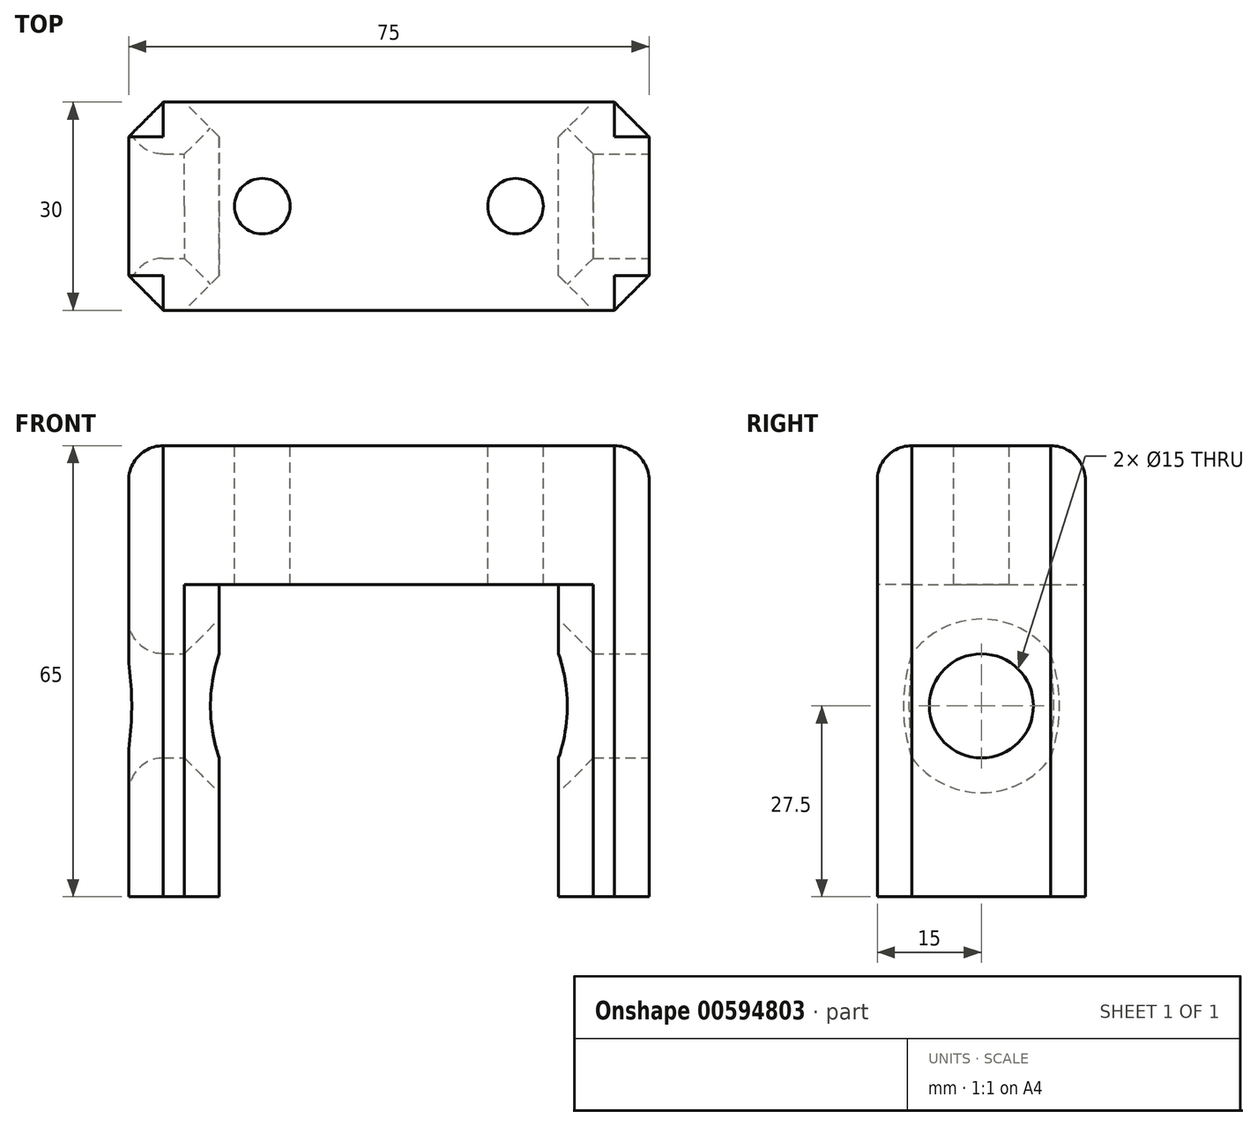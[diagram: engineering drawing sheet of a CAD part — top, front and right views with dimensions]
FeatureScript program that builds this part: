
annotation { "Feature Type Name" : "Feature", "Feature Type Description" : "" }
export const myFeature = defineFeature(function(context is Context, id is Id, definition is map)
    precondition{}
    {
        {
            var Q0;
            Q0=qCreatedBy(makeId("Front.planeOp"),FACE);
            var sketch = newSketch(context, id + "F0", { "sketchPlane" : qUnion([Q0])});
            skLineSegment(sketch, "E0", {"start": v(-41.09, -45) * mm, "end": v(-28.05, -45) * mm});
            skLineSegment(sketch, "E1", {"start": v(-28.05, -45) * mm, "end": v(-28.05, 0) * mm});
            skLineSegment(sketch, "E2", {"start": v(-28.05, 0) * mm, "end": v(20.87, 0) * mm});
            skLineSegment(sketch, "E3", {"start": v(20.87, 0) * mm, "end": v(20.87, -45) * mm});
            skLineSegment(sketch, "E4", {"start": v(20.87, -45) * mm, "end": v(33.91, -45) * mm});
            skLineSegment(sketch, "E5", {"start": v(33.91, -45) * mm, "end": v(33.91, 20) * mm});
            skLineSegment(sketch, "E6", {"start": v(33.91, 20) * mm, "end": v(-41.09, 20) * mm});
            skLineSegment(sketch, "E7", {"start": v(-41.09, 20) * mm, "end": v(-41.09, -45) * mm});
            skSolve(sketch);
        }
        {
            var Q0;
            Q0 = qSketchRegion(id + "F0", true);
            var Q1;
            Q1=sQuery(id+"F0.wireOp",EDGE,"E6");
            var Q2;
            Q2=sQuery(id+"F0.wireOp",EDGE,"E5");
            var Q3;
            Q3=sQuery(id+"F0.wireOp",EDGE,"E3");
            var Q4;
            Q4=sQuery(id+"F0.wireOp",EDGE,"E2");
            var Q5;
            Q5=sQuery(id+"F0.wireOp",EDGE,"E1");
            var Q6;
            Q6=sQuery(id+"F0.wireOp",EDGE,"E7");
            var Q7;
            Q7=sQuery(id+"F0.wireOp",EDGE,"E0");
            var Q8;
            Q8=sQuery(id+"F0.wireOp",EDGE,"E4");
            extrude(context, id + "F1", {"entities" : qUnion([Q0]), "surfaceEntities" : qUnion([Q1, Q2, Q3, Q4, Q5, Q6, Q7, Q8]), "endBound" : BoundingType.SYMMETRIC, "depth" : 30 * mm, "offsetDistance" : 25 * mm});
        }
        {
            var Q0;
            Q0=makeQuery(id+"F1.opExtrude","SWEPT_FACE",FACE,{"disambiguationData":[OSD([sQuery(id+"F0.wireOp",EDGE,"E5")])]});
            var sketch = newSketch(context, id + "F2", { "sketchPlane" : qUnion([Q0])});
            skCircle(sketch, "E8", {"center": v(0, -17.5) * mm, "radius": 7.5 * mm});
            skSolve(sketch);
        }
        {
            var Q0;
            Q0 = qSketchRegion(id + "F2", true);
            extrude(context, id + "F3", {"entities" : qUnion([Q0]), "operationType" : NewBodyOperationType.REMOVE, "oppositeDirection" : true, "depth" : 107 * mm, "offsetDistance" : 25 * mm});
        }
        {
            var Q0;
            Q0=makeQuery(id+"F1.opExtrude","SWEPT_EDGE",EDGE,{"disambiguationData":[OSD([sQuery(id+"F0.wireOp",EDGE,"E5"),sQuery(id+"F0.wireOp",EDGE,"E6")])]});
            var Q1;
            Q1=makeQuery(id+"F1.opExtrude","SWEPT_EDGE",EDGE,{"disambiguationData":[OSD([sQuery(id+"F0.wireOp",EDGE,"E6"),sQuery(id+"F0.wireOp",EDGE,"E7")])]});
            var Q2;
            Q2=makeQuery(id+"F1.opExtrude","CAP_EDGE",EDGE,{"disambiguationData":[OSD([sQuery(id+"F0.wireOp",EDGE,"E6")])],"isStart":true});
            var Q3;
            Q3=makeQuery(id+"F1.opExtrude","CAP_EDGE",EDGE,{"disambiguationData":[OSD([sQuery(id+"F0.wireOp",EDGE,"E6")])],"isStart":false});
            fillet(context, id + "F4", {"entities" : qUnion([Q0, Q1, Q2, Q3]), "radius" : 5 * mm, "tangentPropagation" : true, "allowEdgeOverflow" : false});
        }
        {
            var Q0;
            Q0=makeQuery(id+"F1.opExtrude","CAP_EDGE",EDGE,{"disambiguationData":[OSD([sQuery(id+"F0.wireOp",EDGE,"E5")])],"isStart":true});
            var Q1;
            Q1=makeQuery(id+"F1.opExtrude","CAP_EDGE",EDGE,{"disambiguationData":[OSD([sQuery(id+"F0.wireOp",EDGE,"E5")])],"isStart":false});
            var Q2;
            Q2=makeQuery(id+"F1.opExtrude","CAP_EDGE",EDGE,{"disambiguationData":[OSD([sQuery(id+"F0.wireOp",EDGE,"E3")])],"isStart":false});
            var Q3;
            Q3=makeQuery(id+"F1.opExtrude","CAP_EDGE",EDGE,{"disambiguationData":[OSD([sQuery(id+"F0.wireOp",EDGE,"E3")])],"isStart":true});
            var Q4;
            Q4=makeQuery(id+"F1.opExtrude","CAP_EDGE",EDGE,{"disambiguationData":[OSD([sQuery(id+"F0.wireOp",EDGE,"E7")])],"isStart":false});
            var Q5;
            Q5=makeQuery(id+"F1.opExtrude","CAP_EDGE",EDGE,{"disambiguationData":[OSD([sQuery(id+"F0.wireOp",EDGE,"E7")])],"isStart":true});
            var Q6;
            Q6=makeQuery(id+"F1.opExtrude","CAP_EDGE",EDGE,{"disambiguationData":[OSD([sQuery(id+"F0.wireOp",EDGE,"E1")])],"isStart":true});
            var Q7;
            Q7=makeQuery(id+"F1.opExtrude","CAP_EDGE",EDGE,{"disambiguationData":[OSD([sQuery(id+"F0.wireOp",EDGE,"E1")])],"isStart":false});
            chamfer(context, id + "F5", {"entities" : qUnion([Q0, Q1, Q2, Q3, Q4, Q5, Q6, Q7]), "width" : 5 * mm, "tangentPropagation" : true});
        }
        {
            var Q0;
            Q0=makeQuery(id+"F3.boolean.opBoolean","INTERSECT",EDGE,{"derivedFrom":[makeQuery(id+"F1.opExtrude","SWEPT_FACE",FACE,{"disambiguationData":[OSD([sQuery(id+"F0.wireOp",EDGE,"E7")])]}),makeQuery(id+"F3.opExtrude","SWEPT_FACE",FACE,{"disambiguationData":[OSD([sQuery(id+"F2.wireOp",EDGE,"E8")])]})]});
            var Q1;
            Q1=makeQuery(id+"F3.boolean.opBoolean","COPY",EDGE,{"derivedFrom":makeQuery(id+"F3.opExtrude","CAP_EDGE",EDGE,{"disambiguationData":[OSD([sQuery(id+"F2.wireOp",EDGE,"E8")])],"isStart":true})});
            var Q2;
            Q2=makeQuery(id+"F3.boolean.opBoolean","COPY",EDGE,{"derivedFrom":makeQuery(id+"F3.opExtrude","CAP_EDGE",EDGE,{"disambiguationData":[OSD([sQuery(id+"F2.wireOp",EDGE,"E8")])],"isStart":true})});
            fillet(context, id + "F6", {"entities" : qUnion([Q0, Q1, Q2]), "radius" : 5 * mm, "tangentPropagation" : true, "allowEdgeOverflow" : false});
        }
        {
            var Q0;
            Q0=makeQuery(id+"F3.boolean.opBoolean","INTERSECT",EDGE,{"derivedFrom":[makeQuery(id+"F1.opExtrude","SWEPT_FACE",FACE,{"disambiguationData":[OSD([sQuery(id+"F0.wireOp",EDGE,"E1")])]}),makeQuery(id+"F3.opExtrude","SWEPT_FACE",FACE,{"disambiguationData":[OSD([sQuery(id+"F2.wireOp",EDGE,"E8")])]})]});
            var Q1;
            Q1=makeQuery(id+"F3.boolean.opBoolean","INTERSECT",EDGE,{"derivedFrom":[makeQuery(id+"F1.opExtrude","SWEPT_FACE",FACE,{"disambiguationData":[OSD([sQuery(id+"F0.wireOp",EDGE,"E3")])]}),makeQuery(id+"F3.opExtrude","SWEPT_FACE",FACE,{"disambiguationData":[OSD([sQuery(id+"F2.wireOp",EDGE,"E8")])]})]});
            chamfer(context, id + "F7", {"entities" : qUnion([Q0, Q1]), "width" : 5 * mm, "tangentPropagation" : true});
        }
        {
            var Q0;
            Q0=makeQuery(id+"F1.opExtrude","SWEPT_FACE",FACE,{"disambiguationData":[OSD([sQuery(id+"F0.wireOp",EDGE,"E6")])]});
            var sketch = newSketch(context, id + "F8", { "sketchPlane" : qUnion([Q0])});
            skCircle(sketch, "E9", {"center": v(-21.84, 0) * mm, "radius": 4 * mm});
            skCircle(sketch, "E10", {"center": v(14.66, 0) * mm, "radius": 4 * mm});
            skLineSegment(sketch, "E11", {"start": v(-21.84, 0) * mm, "end": v(14.66, 0) * mm, "construction": true});
            skSolve(sketch);
        }
        {
            var Q0;
            Q0 = qSketchRegion(id + "F8", true);
            extrude(context, id + "F9", {"entities" : qUnion([Q0]), "operationType" : NewBodyOperationType.REMOVE, "oppositeDirection" : true, "depth" : 21.4 * mm, "offsetDistance" : 25 * mm});
        }
    });
